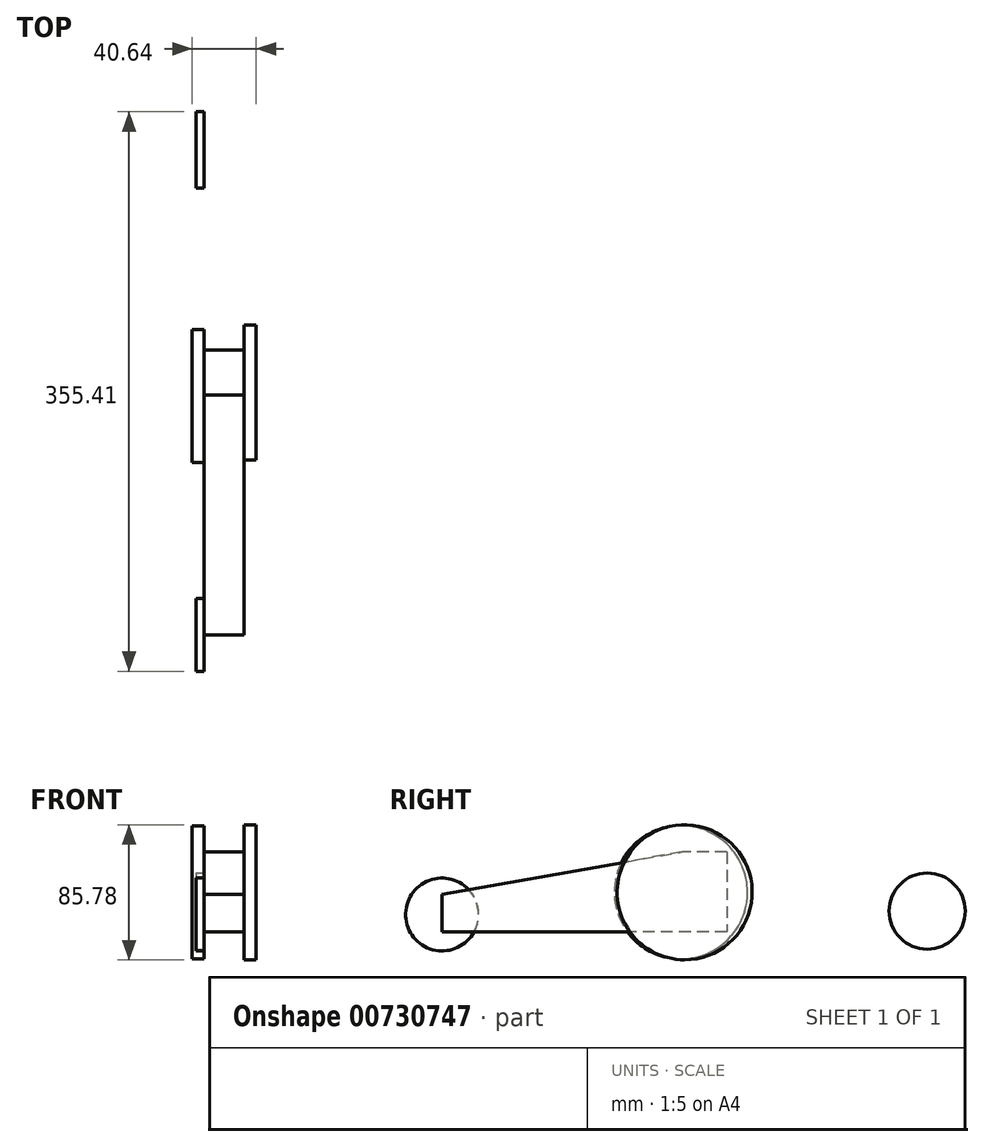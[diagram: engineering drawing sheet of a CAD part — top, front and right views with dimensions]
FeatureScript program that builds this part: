
annotation { "Feature Type Name" : "Feature", "Feature Type Description" : "" }
export const myFeature = defineFeature(function(context is Context, id is Id, definition is map)
    precondition{}
    {
        {
            var Q0;
            Q0=qCreatedBy(makeId("Right.planeOp"),FACE);
            var sketch = newSketch(context, id + "F0", { "sketchPlane" : qUnion([Q0])});
            skCircle(sketch, "E0", {"center": v(0, 0) * mm, "radius": 42.9 * mm});
            skSolve(sketch);
        }
        {
            var Q0;
            Q0 = qSketchRegion(id + "F0", true);
            extrude(context, id + "F1", {"entities" : qUnion([Q0]), "depth" : 7.62 * mm, "offsetDistance" : 25.4 * mm});
        }
        {
            var Q0;
            Q0=makeQuery(id+"F1.opExtrude","CAP_FACE",FACE,{"disambiguationData":[OSD([sQuery(id+"F0.wireOp",EDGE,"E0")])],"isStart":true});
            var sketch = newSketch(context, id + "F2", { "sketchPlane" : qUnion([Q0])});
            skLineSegment(sketch, "E1.bottom", {"start": v(-26.89, 25.62) * mm, "end": v(27.05, 25.62) * mm});
            skLineSegment(sketch, "E1.top", {"start": v(-26.89, -25.18) * mm, "end": v(27.05, -25.18) * mm});
            skLineSegment(sketch, "E1.left", {"start": v(-26.89, 25.62) * mm, "end": v(-26.89, -25.18) * mm});
            skLineSegment(sketch, "E1.right", {"start": v(27.05, 25.62) * mm, "end": v(27.05, -25.18) * mm});
            skSolve(sketch);
        }
        {
            var Q0;
            Q0 = qSketchRegion(id + "F2", true);
            extrude(context, id + "F3", {"entities" : qUnion([Q0]), "operationType" : NewBodyOperationType.ADD, "depth" : 25.4 * mm, "offsetDistance" : 25.4 * mm});
        }
        {
            var Q0;
            Q0=makeQuery(id+"F3.opExtrude","SWEPT_FACE",FACE,{"disambiguationData":[OSD([sQuery(id+"F2.wireOp",EDGE,"E1.right")])]});
            extrude(context, id + "F4", {"entities" : qUnion([Q0]), "operationType" : NewBodyOperationType.ADD, "depth" : 127 * mm, "offsetDistance" : 25.4 * mm});
        }
        {
            var Q0;
            {var subQ0=sQuery(id+"F2.wireOp",EDGE,"E1.right");Q0=makeQuery(id+"F4.boolean.opBoolean","MERGE",FACE,{"derivedFrom":[makeQuery(id+"F3.opExtrude","CAP_FACE",FACE,{"disambiguationData":[OSD([sQuery(id+"F2.wireOp",EDGE,"E1.bottom"),sQuery(id+"F2.wireOp",EDGE,"E1.top"),sQuery(id+"F2.wireOp",EDGE,"E1.left"),subQ0])],"isStart":false}),makeQuery(id+"F4.opExtrude","SWEPT_FACE",FACE,{"disambiguationData":[OSD([subQ0]),TDD([makeQuery(id+"F3.opExtrude","CAP_EDGE",EDGE,{"disambiguationData":[OSD([subQ0])],"isStart":false})])]})]});}
            var sketch = newSketch(context, id + "F5", { "sketchPlane" : qUnion([Q0])});
            skCircle(sketch, "E2", {"center": v(2.36, 0) * mm, "radius": 42.33 * mm});
            skSolve(sketch);
        }
        {
            var Q0;
            Q0 = qSketchRegion(id + "F5", true);
            extrude(context, id + "F6", {"entities" : qUnion([Q0]), "operationType" : NewBodyOperationType.ADD, "depth" : 7.62 * mm, "offsetDistance" : 25.4 * mm});
        }
        {
            var Q0;
            {var subQ0=sQuery(id+"F2.wireOp",EDGE,"E1.right");Q0=makeQuery(id+"F4.boolean.opBoolean","MERGE",FACE,{"derivedFrom":[makeQuery(id+"F3.opExtrude","CAP_FACE",FACE,{"disambiguationData":[OSD([sQuery(id+"F2.wireOp",EDGE,"E1.bottom"),sQuery(id+"F2.wireOp",EDGE,"E1.top"),sQuery(id+"F2.wireOp",EDGE,"E1.left"),subQ0])],"isStart":false}),makeQuery(id+"F4.opExtrude","SWEPT_FACE",FACE,{"disambiguationData":[OSD([subQ0]),TDD([makeQuery(id+"F3.opExtrude","CAP_EDGE",EDGE,{"disambiguationData":[OSD([subQ0])],"isStart":false})])]})]});}
            var sketch = newSketch(context, id + "F7", { "sketchPlane" : qUnion([Q0])});
            skCircle(sketch, "E3", {"center": v(154.05, -14.1) * mm, "radius": 23.14 * mm});
            skSolve(sketch);
        }
        {
            var Q0;
            Q0 = qSketchRegion(id + "F7", true);
            extrude(context, id + "F8", {"entities" : qUnion([Q0]), "operationType" : NewBodyOperationType.ADD, "depth" : 5.08 * mm, "offsetDistance" : 25.4 * mm});
        }
        {
            var Q0;
            {var subQ0=sQuery(id+"F2.wireOp",EDGE,"E1.right");Q0=makeQuery(id+"F4.opExtrude","SWEPT_FACE",FACE,{"disambiguationData":[OSD([subQ0]),TDD([makeQuery(id+"F3.opExtrude","CAP_EDGE",EDGE,{"disambiguationData":[OSD([subQ0])],"isStart":true})])]});}
            var sketch = newSketch(context, id + "F9", { "sketchPlane" : qUnion([Q0])});
            skCircle(sketch, "E4", {"center": v(-154.05, -11.92) * mm, "radius": 24.18 * mm});
            skSolve(sketch);
        }
        {
            var Q0;
            Q0 = qSketchRegion(id + "F9", true);
            extrude(context, id + "F10", {"entities" : qUnion([Q0]), "operationType" : NewBodyOperationType.ADD, "depth" : 5.08 * mm, "offsetDistance" : 25.4 * mm});
        }
        {
            var Q0;
            Q0=makeQuery(id+"F4.opExtrude","CAP_EDGE",EDGE,{"disambiguationData":[OSD([sQuery(id+"F2.wireOp",EDGE,"E1.bottom"),sQuery(id+"F2.wireOp",EDGE,"E1.right")])],"isStart":false});
            chamfer(context, id + "F11", {"entities" : qUnion([Q0]), "chamferType" : ChamferType.OFFSET_ANGLE, "width" : 152.4 * mm, "oppositeDirection" : false, "angle" : 10 * degree, "tangentPropagation" : true});
        }
    });
